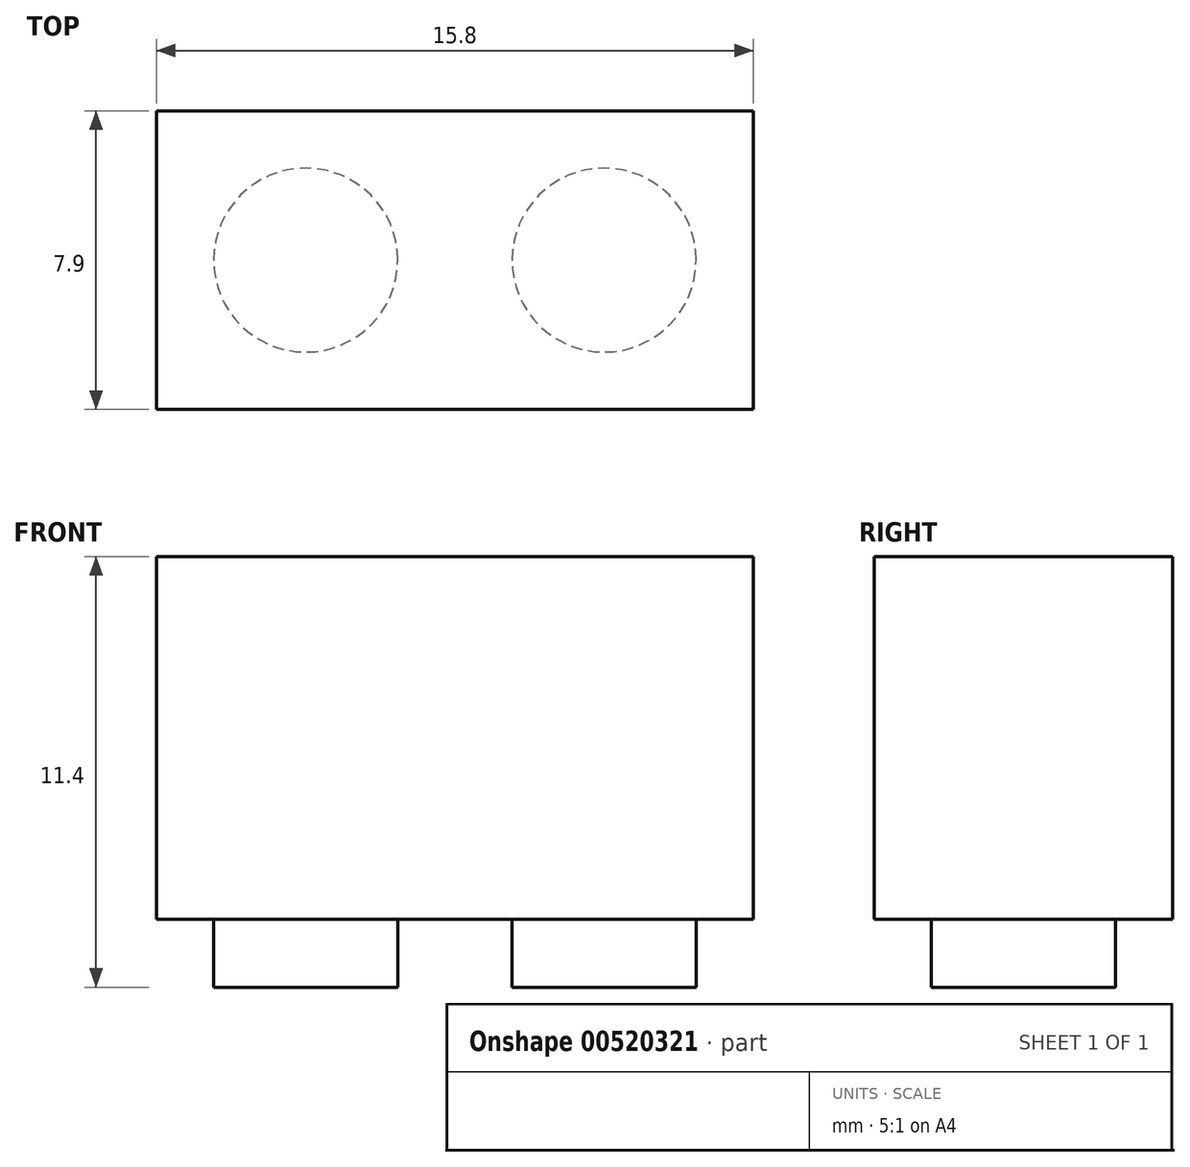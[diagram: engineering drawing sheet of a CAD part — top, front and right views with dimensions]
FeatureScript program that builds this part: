
annotation { "Feature Type Name" : "Feature", "Feature Type Description" : "" }
export const myFeature = defineFeature(function(context is Context, id is Id, definition is map)
    precondition{}
    {
        {
            var Q0;
            Q0=qCreatedBy(makeId("Top.planeOp"),FACE);
            var sketch = newSketch(context, id + "F0", { "sketchPlane" : qUnion([Q0])});
            skLineSegment(sketch, "E0.bottom", {"start": v(-7.9, 3.95) * mm, "end": v(7.9, 3.95) * mm});
            skLineSegment(sketch, "E0.top", {"start": v(-7.9, -3.95) * mm, "end": v(7.9, -3.95) * mm});
            skLineSegment(sketch, "E0.left", {"start": v(-7.9, 3.95) * mm, "end": v(-7.9, -3.95) * mm});
            skLineSegment(sketch, "E0.right", {"start": v(7.9, 3.95) * mm, "end": v(7.9, -3.95) * mm});
            skPoint(sketch, "E0.middle", {"position": v(0, 0) * mm});
            skSolve(sketch);
        }
        {
            var Q0;
            Q0 = qSketchRegion(id + "F0", true);
            extrude(context, id + "F1", {"entities" : qUnion([Q0]), "depth" : 9.6 * mm, "offsetDistance" : 25 * mm});
        }
        {
            var Q0;
            Q0=makeQuery(id+"F1.opExtrude","CAP_FACE",FACE,{"disambiguationData":[OSD([sQuery(id+"F0.wireOp",EDGE,"E0.bottom"),sQuery(id+"F0.wireOp",EDGE,"E0.top"),sQuery(id+"F0.wireOp",EDGE,"E0.left"),sQuery(id+"F0.wireOp",EDGE,"E0.right")])],"isStart":false});
            var sketch = newSketch(context, id + "F2", { "sketchPlane" : qUnion([Q0])});
            skCircle(sketch, "E1", {"center": v(-3.95, 0) * mm, "radius": 2.44 * mm});
            skPoint(sketch, "E1.centerSnap0", {"position": v(-3.95, -3.95) * mm});
            skCircle(sketch, "E2.MirrorC", {"center": v(3.95, 0) * mm, "radius": 2.44 * mm});
            skPoint(sketch, "E3.start.orphan", {"position": v(0, 3.95) * mm});
            skPoint(sketch, "E4.orphan", {"position": v(0, -3.95) * mm});
            skPoint(sketch, "E5.end.orphan", {"position": v(-7.9, -3.95) * mm});
            skSolve(sketch);
        }
        {
            var Q0;
            Q0 = qSketchRegion(id + "F2", true);
            extrude(context, id + "F3", {"entities" : qUnion([Q0]), "operationType" : NewBodyOperationType.ADD, "oppositeDirection" : true, "depth" : 11.4 * mm, "offsetDistance" : 25 * mm});
        }
    });
